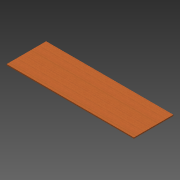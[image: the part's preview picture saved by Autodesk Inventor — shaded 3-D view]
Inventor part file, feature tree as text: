
AUTODESK INVENTOR PART (.ipt)
format: ipt  version: 2013 (Build 170138000, 138)  size: 76,800 bytes
history: native  units: in
note: dims shown in document units (in); Inventor stores cm internally (conversion verified against a paired STEP export)
features: extrude x1, sketch x1
ambient origin geometry x8: Origin, YZ Plane, XZ Plane, XY Plane, X Axis, Y Axis, Z Axis, Center Point
bodies: Solid1 (feature_tree)
feature tree (2):
  extrude  "Extrusion1"  Depth=18.0in
  sketch  "Sketch1"  dims[d0=58.0in d1=18.0in d2=0.5in d3=0.0in]
